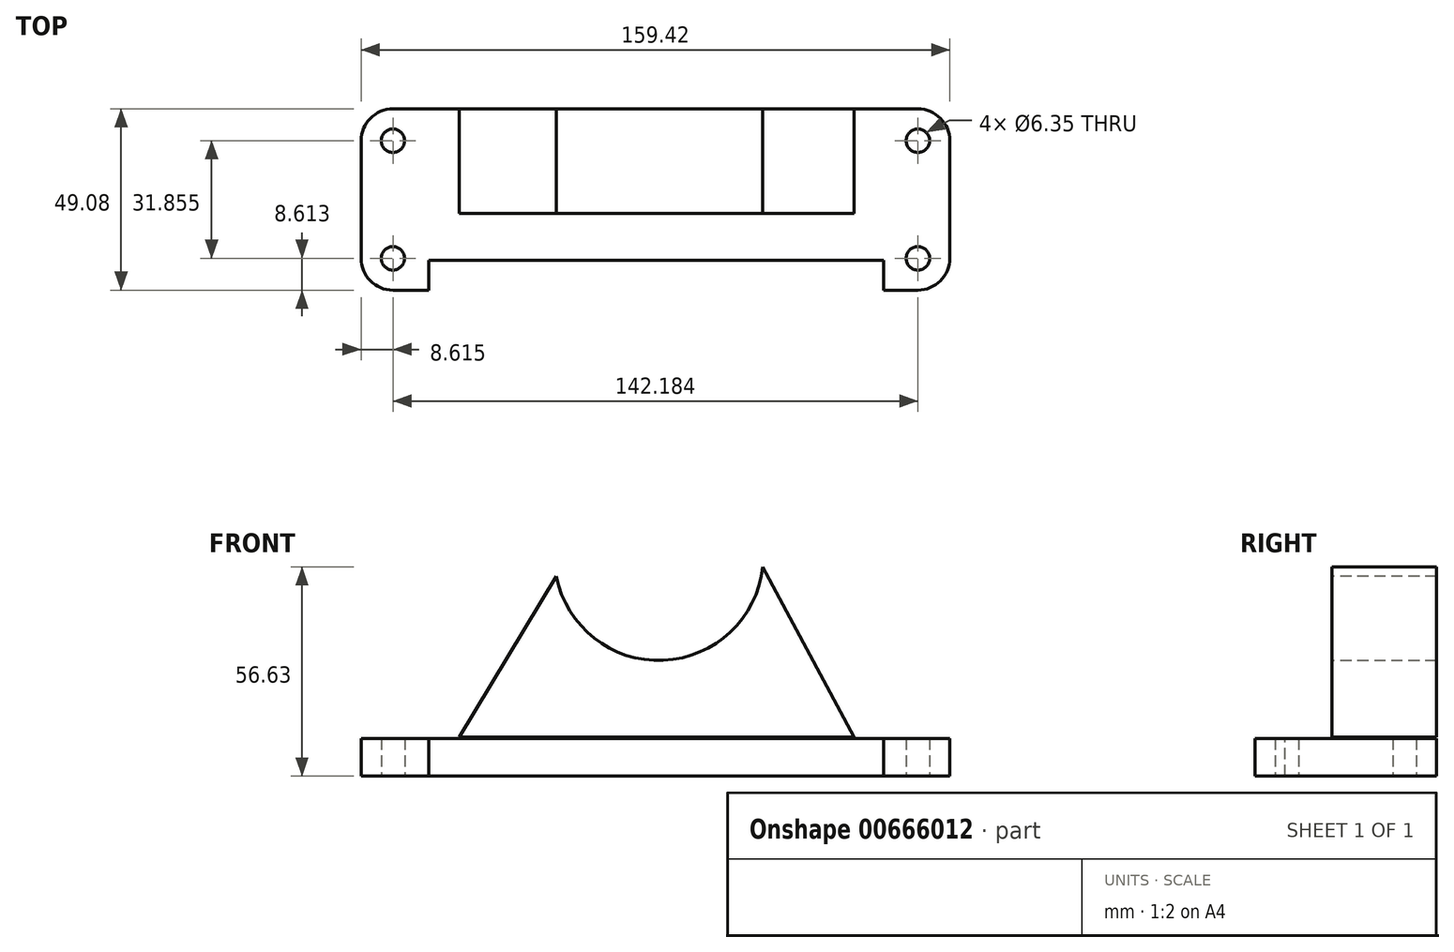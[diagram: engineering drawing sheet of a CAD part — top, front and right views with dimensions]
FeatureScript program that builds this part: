
annotation { "Feature Type Name" : "Feature", "Feature Type Description" : "" }
export const myFeature = defineFeature(function(context is Context, id is Id, definition is map)
    precondition{}
    {
        {
            var Q0;
            Q0=qCreatedBy(makeId("Top.planeOp"),FACE);
            var sketch = newSketch(context, id + "F0", { "sketchPlane" : qUnion([Q0])});
            skLineSegment(sketch, "E0.bottom", {"start": v(-35.85, 26.97) * mm, "end": v(106.33, 26.97) * mm});
            skLineSegment(sketch, "E0.top", {"start": v(-35.85, -22.11) * mm, "end": v(106.33, -22.11) * mm});
            skLineSegment(sketch, "E0.left", {"start": v(-44.47, 18.36) * mm, "end": v(-44.47, -13.5) * mm});
            skLineSegment(sketch, "E0.right", {"start": v(114.95, 18.36) * mm, "end": v(114.95, -13.5) * mm});
            skPoint(sketch, "E1.visualSharp", {"position": v(114.95, 26.97) * mm});
            skArc(sketch, "E1.filletArc", {"start": v(114.95, 18.36) * mm, "mid": v(112.42, 24.45) * mm, "end": v(106.33, 26.97) * mm});
            skPoint(sketch, "E2.visualSharp", {"position": v(114.95, -22.11) * mm});
            skArc(sketch, "E2.filletArc", {"start": v(106.33, -22.11) * mm, "mid": v(112.42, -19.6) * mm, "end": v(114.95, -13.5) * mm});
            skPoint(sketch, "E3.visualSharp", {"position": v(-44.47, -22.11) * mm});
            skArc(sketch, "E3.filletArc", {"start": v(-44.47, -13.5) * mm, "mid": v(-41.95, -19.6) * mm, "end": v(-35.85, -22.11) * mm});
            skPoint(sketch, "E4.visualSharp", {"position": v(-44.47, 26.97) * mm});
            skArc(sketch, "E4.filletArc", {"start": v(-35.85, 26.97) * mm, "mid": v(-41.95, 24.45) * mm, "end": v(-44.47, 18.36) * mm});
            skSolve(sketch);
        }
        {
            var Q0;
            Q0=makeQuery(id+"F0.imprint","IMPRINT",FACE,{"disambiguationData":[TD([[makeQuery(id+"F0.imprint","IMPRINT",EDGE,{"derivedFrom":sQuery(id+"F0.wireOp",EDGE,"E0.bottom")}),-1.0]])]});
            var sketch = newSketch(context, id + "F1", { "sketchPlane" : qUnion([Q0])});
            skSolve(sketch);
        }
        {
            var Q0;
            Q0=makeQuery(id+"F1.imprint","IMPRINT",FACE,{"disambiguationData":[TD([[makeQuery(id+"F1.imprint","IMPRINT",EDGE,{"derivedFrom":makeQuery(id+"F0.imprint","IMPRINT",EDGE,{"derivedFrom":sQuery(id+"F0.wireOp",EDGE,"E0.bottom")})}),-1.0]])]});
            extrude(context, id + "F2", {"entities" : qUnion([Q0]), "depth" : 10.16 * mm, "offsetDistance" : 25.4 * mm});
        }
        {
            var Q0;
            Q0=makeQuery(id+"F2.opExtrude","CAP_FACE",FACE,{"disambiguationData":[OSD([sQuery(id+"F0.wireOp",EDGE,"E0.bottom"),sQuery(id+"F0.wireOp",EDGE,"E0.top"),sQuery(id+"F0.wireOp",EDGE,"E0.left"),sQuery(id+"F0.wireOp",EDGE,"E0.right"),sQuery(id+"F0.wireOp",EDGE,"E1.filletArc"),sQuery(id+"F0.wireOp",EDGE,"E2.filletArc"),sQuery(id+"F0.wireOp",EDGE,"E3.filletArc"),sQuery(id+"F0.wireOp",EDGE,"E4.filletArc")])],"isStart":false});
            var sketch = newSketch(context, id + "F3", { "sketchPlane" : qUnion([Q0])});
            skLineSegment(sketch, "E5.bottom", {"start": v(-26.08, -13.98) * mm, "end": v(97.03, -13.98) * mm});
            skLineSegment(sketch, "E5.top", {"start": v(-26.08, -42.37) * mm, "end": v(97.03, -42.37) * mm});
            skLineSegment(sketch, "E5.left", {"start": v(-26.08, -13.98) * mm, "end": v(-26.08, -42.37) * mm});
            skLineSegment(sketch, "E5.right", {"start": v(97.03, -13.98) * mm, "end": v(97.03, -42.37) * mm});
            skSolve(sketch);
        }
        {
            var Q0;
            Q0 = qSketchRegion(id + "F3", true);
            extrude(context, id + "F4", {"entities" : qUnion([Q0]), "operationType" : NewBodyOperationType.REMOVE, "endBound" : BoundingType.THROUGH_ALL, "oppositeDirection" : true, "depth" : 25.4 * mm, "offsetDistance" : 25.4 * mm});
        }
        {
            var Q0;
            Q0=sQuery(id+"F0.wireOp",VERTEX,"E1.filletArc.center");
            var Q1;
            Q1=sQuery(id+"F0.wireOp",VERTEX,"E2.filletArc.center");
            var Q2;
            Q2=sQuery(id+"F0.wireOp",VERTEX,"E3.filletArc.center");
            var Q3;
            Q3=sQuery(id+"F0.wireOp",VERTEX,"E4.filletArc.center");
            var Q4;
            Q4=makeQuery(id+"F2.opExtrude","SWEPT_BODY",BODY,{"disambiguationData":[OSD([sQuery(id+"F0.wireOp",EDGE,"E0.bottom"),sQuery(id+"F0.wireOp",EDGE,"E0.top"),sQuery(id+"F0.wireOp",EDGE,"E0.left"),sQuery(id+"F0.wireOp",EDGE,"E0.right"),sQuery(id+"F0.wireOp",EDGE,"E1.filletArc"),sQuery(id+"F0.wireOp",EDGE,"E2.filletArc"),sQuery(id+"F0.wireOp",EDGE,"E3.filletArc"),sQuery(id+"F0.wireOp",EDGE,"E4.filletArc")])]});
            hole(context, id + "F5", {"style" : HoleStyle.SIMPLE, "endStyle" : HoleEndStyle.THROUGH, "oppositeDirection" : true, "holeDiameter" : 6.35 * mm, "majorDiameter" : 6.35 * mm, "isTappedThrough" : true, "tappedDepth" : 12.7 * mm, "tapClearance" : 3, "locations" : qUnion([Q0, Q1, Q2, Q3]), "scope" : qUnion([Q4])});
        }
        {
            var Q0;
            Q0=makeQuery(id+"F4.boolean.opBoolean","COPY",FACE,{"derivedFrom":makeQuery(id+"F4.opExtrude","SWEPT_FACE",FACE,{"disambiguationData":[OSD([sQuery(id+"F3.wireOp",EDGE,"E5.bottom")])]})});
            cPlane(context, id + "F6", {"entities" : qUnion([Q0]), "cplaneType" : CPlaneType.OFFSET, "offset" : 12.7 * mm, "oppositeDirection" : true, "width" : 152.4 * mm, "height" : 152.4 * mm});
        }
        {
            var Q0;
            Q0=qCreatedBy(id+"F6.planeOp",FACE);
            var sketch = newSketch(context, id + "F7", { "sketchPlane" : qUnion([Q0])});
            skLineSegment(sketch, "E6", {"start": v(-17.95, 10.5) * mm, "end": v(89.07, 10.5) * mm});
            skLineSegment(sketch, "E7", {"start": v(89.07, 10.5) * mm, "end": v(64.26, 56.63) * mm});
            skLineSegment(sketch, "E8", {"start": v(-17.95, 10.5) * mm, "end": v(8.41, 54.12) * mm});
            skArc(sketch, "E9", {"start": v(8.41, 54.12) * mm, "mid": v(37.42, 31.32) * mm, "end": v(64.26, 56.63) * mm});
            skSolve(sketch);
        }
        {
            var Q0;
            Q0=makeQuery(id+"F7.imprint","IMPRINT",FACE,{"disambiguationData":[TD([[makeQuery(id+"F7.imprint","IMPRINT",EDGE,{"derivedFrom":sQuery(id+"F7.wireOp",EDGE,"E6")}),1.0]])]});
            var Q1;
            Q1=makeQuery(id+"F2.opExtrude","SWEPT_FACE",FACE,{"disambiguationData":[OSD([sQuery(id+"F0.wireOp",EDGE,"E0.bottom")])]});
            extrude(context, id + "F8", {"entities" : qUnion([Q0]), "endBound" : BoundingType.UP_TO_SURFACE, "oppositeDirection" : true, "depth" : 25.4 * mm, "endBoundEntityFace" : qUnion([Q1]), "offsetDistance" : 25.4 * mm});
        }
    });
